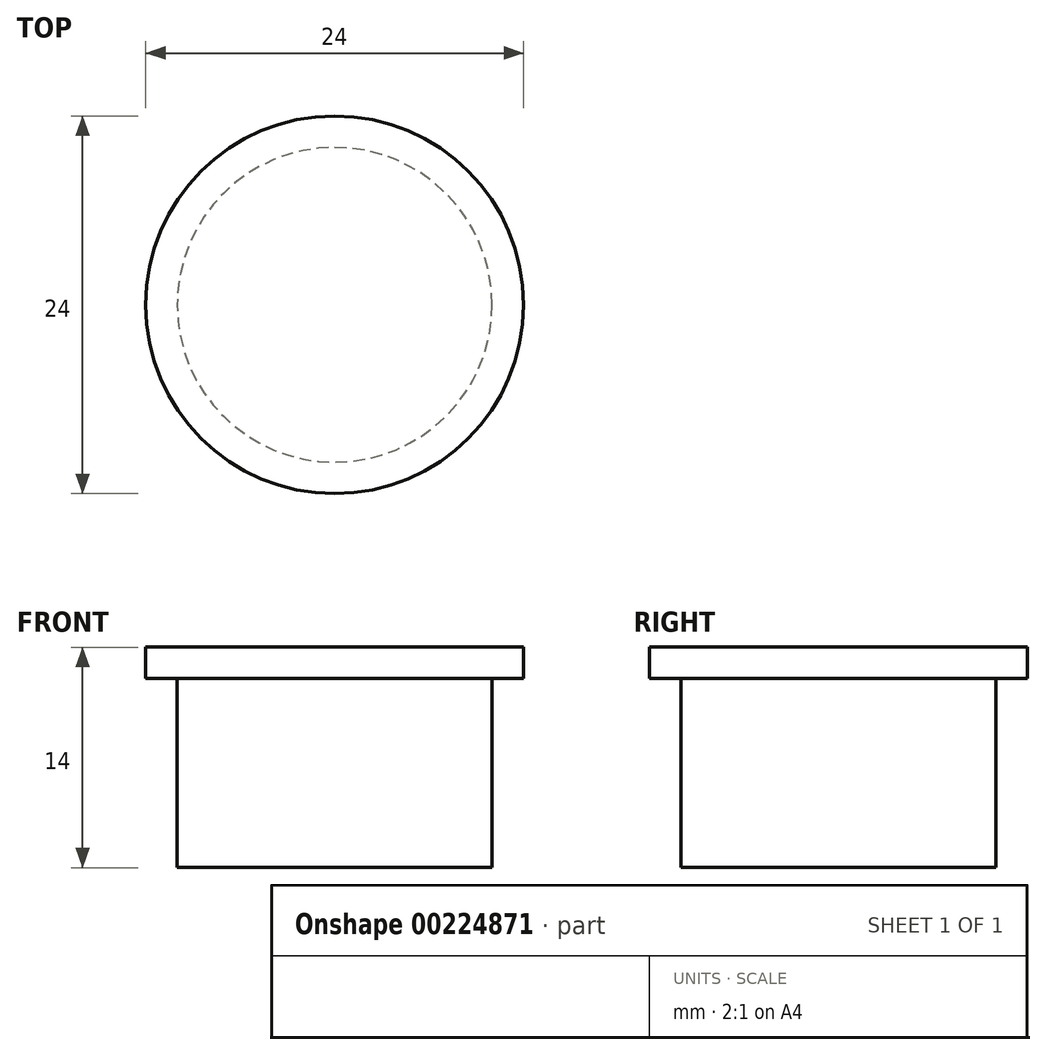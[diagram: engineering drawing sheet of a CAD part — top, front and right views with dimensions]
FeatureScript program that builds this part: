
annotation { "Feature Type Name" : "Feature", "Feature Type Description" : "" }
export const myFeature = defineFeature(function(context is Context, id is Id, definition is map)
    precondition{}
    {
        {
            var Q0;
            Q0=qCreatedBy(makeId("Right.planeOp"),FACE);
            var sketch = newSketch(context, id + "F0", { "sketchPlane" : qUnion([Q0])});
            skLineSegment(sketch, "E0", {"start": v(-10, 6.34) * mm, "end": v(-12, 6.34) * mm});
            skLineSegment(sketch, "E1", {"start": v(-12, 6.34) * mm, "end": v(-12, 8.34) * mm});
            skLineSegment(sketch, "E2", {"start": v(-12, 8.34) * mm, "end": v(0, 8.34) * mm});
            skLineSegment(sketch, "E3", {"start": v(-10, -5.66) * mm, "end": v(0, -5.66) * mm});
            skLineSegment(sketch, "E4", {"start": v(0, -5.66) * mm, "end": v(0, 8.34) * mm});
            skLineSegment(sketch, "E5", {"start": v(-10, 6.34) * mm, "end": v(-10, -5.66) * mm});
            skSolve(sketch);
        }
        {
            var Q0;
            Q0=makeQuery(id+"F0.imprint","IMPRINT",FACE,{"disambiguationData":[TD([[makeQuery(id+"F0.imprint","IMPRINT",EDGE,{"derivedFrom":sQuery(id+"F0.wireOp",EDGE,"E0")}),-1.0]])]});
            var Q1;
            Q1=sQuery(id+"F0.wireOp",EDGE,"E4");
            revolve(context, id + "F1", {"entities" : qUnion([Q0]), "axis" : qUnion([Q1]), "revolveType" : RevolveType.FULL});
        }
    });
